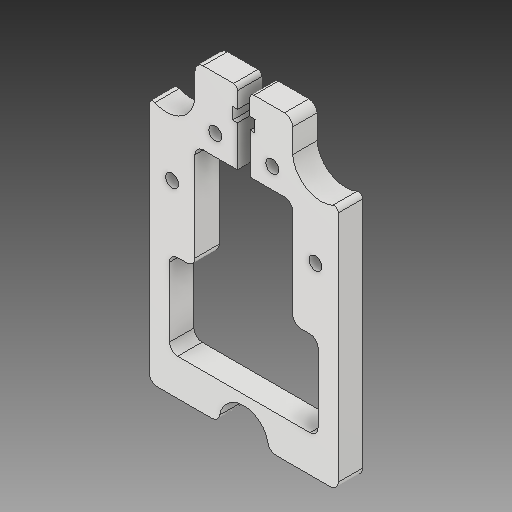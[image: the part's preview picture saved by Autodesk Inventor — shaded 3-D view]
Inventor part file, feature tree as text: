
AUTODESK INVENTOR PART (.ipt)
format: ipt  version: 2017 (Build 210142000, 142)  size: 198,656 bytes
history: native  units: mm
features: other x3, sketch x2
ambient origin geometry x8: Origin, YZ Plane, XZ Plane, XY Plane, X Axis, Y Axis, Z Axis, Center Point
bodies: Solid1 (feature_tree)
feature tree (5):
  other  "Hotend Slide Part 2_MIR.ipt"
  other  "Solid1::Hotend Slide Part 2_MIR.ipt"
  other  "TaggingFeature1"
  sketch  "Sketch1"  dims[d0=10.0mm]
  sketch  "Sketch2"
